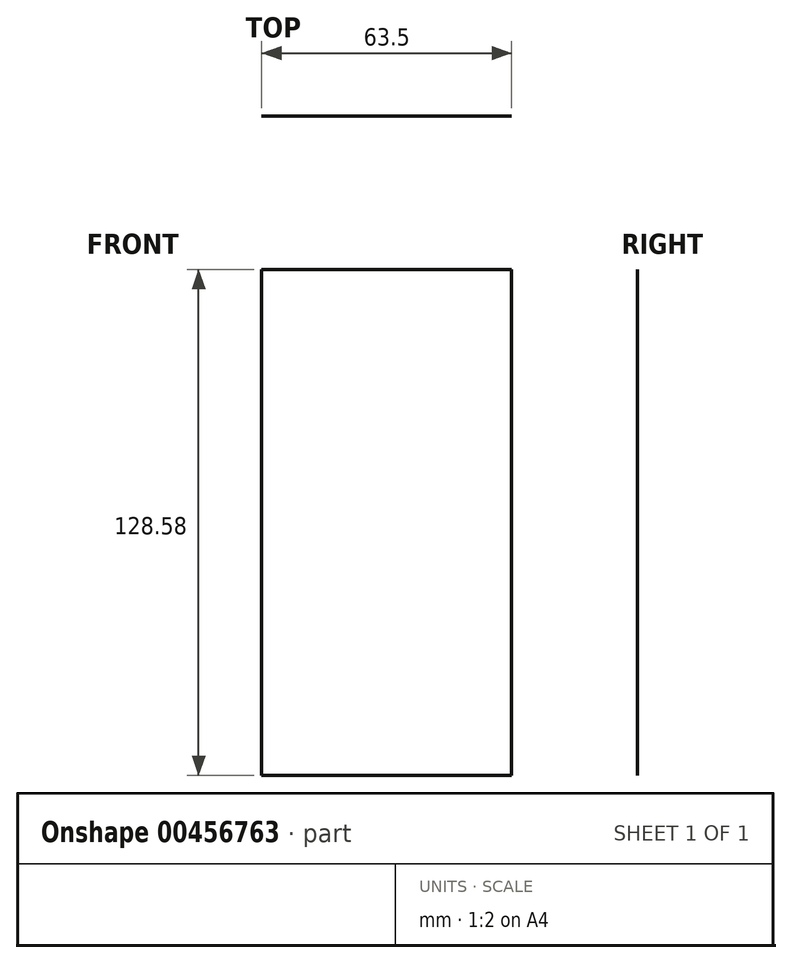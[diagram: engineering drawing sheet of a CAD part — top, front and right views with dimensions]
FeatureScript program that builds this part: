
annotation { "Feature Type Name" : "Feature", "Feature Type Description" : "" }
export const myFeature = defineFeature(function(context is Context, id is Id, definition is map)
    precondition{}
    {
        {
            var Q0;
            Q0=qCreatedBy(makeId("Front.planeOp"),FACE);
            var sketch = newSketch(context, id + "F0", { "sketchPlane" : qUnion([Q0])});
            skLineSegment(sketch, "E0.bottom", {"start": v(-31.75, 64.29) * mm, "end": v(31.75, 64.29) * mm});
            skLineSegment(sketch, "E0.top", {"start": v(-31.75, -64.29) * mm, "end": v(31.75, -64.29) * mm});
            skLineSegment(sketch, "E0.left", {"start": v(-31.75, 64.29) * mm, "end": v(-31.75, -64.29) * mm});
            skLineSegment(sketch, "E0.right", {"start": v(31.75, 64.29) * mm, "end": v(31.75, -64.29) * mm});
            skPoint(sketch, "E0.middle", {"position": v(0, 0) * mm});
            skSolve(sketch);
        }
        {
            var Q0;
            Q0 = qSketchRegion(id + "F0", true);
            extrude(context, id + "F1", {"entities" : qUnion([Q0]), "depth" : 1 / 203.2 * mm});
        }
    });
